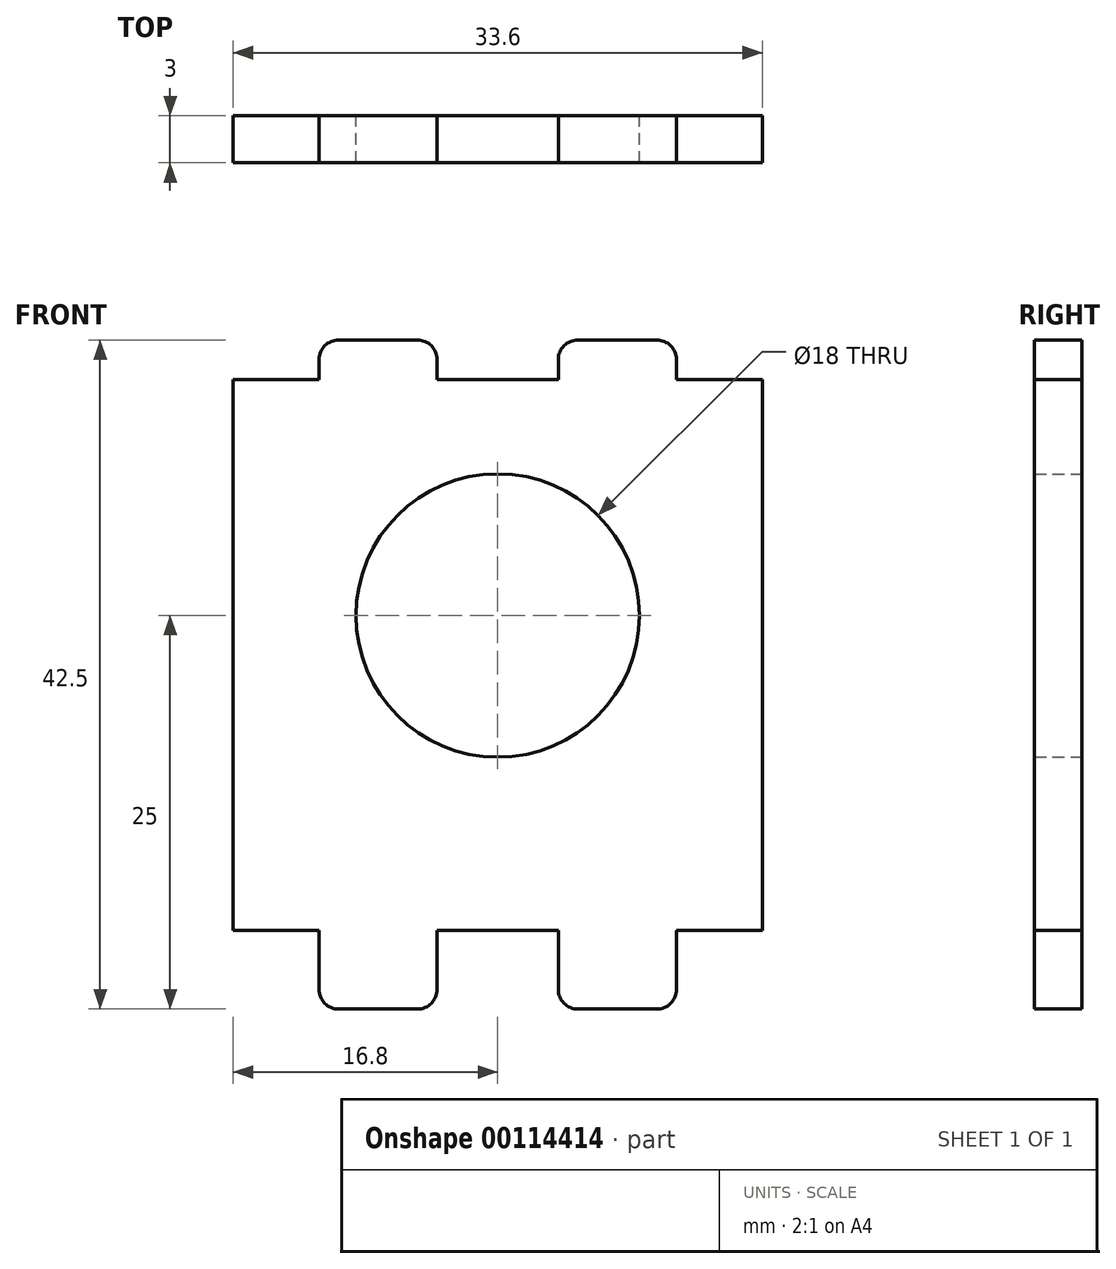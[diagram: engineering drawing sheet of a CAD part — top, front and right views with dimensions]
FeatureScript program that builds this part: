
annotation { "Feature Type Name" : "Feature", "Feature Type Description" : "" }
export const myFeature = defineFeature(function(context is Context, id is Id, definition is map)
    precondition{}
    {
        {
            var Q0;
            Q0=qCreatedBy(makeId("Front.planeOp"),FACE);
            var sketch = newSketch(context, id + "F0", { "sketchPlane" : qUnion([Q0])});
            skLineSegment(sketch, "E0.bottom", {"start": v(-16.8, 17.5) * mm, "end": v(-11.35, 17.5) * mm});
            skLineSegment(sketch, "E0.top", {"start": v(-16.8, -17.5) * mm, "end": v(-11.35, -17.5) * mm});
            skLineSegment(sketch, "E0.left", {"start": v(-16.8, 17.5) * mm, "end": v(-16.8, -17.5) * mm});
            skLineSegment(sketch, "E0.right", {"start": v(16.8, 17.5) * mm, "end": v(16.8, -17.5) * mm});
            skPoint(sketch, "E0.middle", {"position": v(0, 0) * mm});
            skLineSegment(sketch, "E1", {"start": v(-11.35, 18.75) * mm, "end": v(-11.35, 17.5) * mm});
            skLineSegment(sketch, "E2", {"start": v(11.35, 18.75) * mm, "end": v(11.35, 17.5) * mm});
            skLineSegment(sketch, "E3", {"start": v(-11.35, -17.5) * mm, "end": v(-11.35, -21.25) * mm});
            skLineSegment(sketch, "E4", {"start": v(11.35, -17.5) * mm, "end": v(11.35, -21.25) * mm});
            skLineSegment(sketch, "E5.trimOffspring", {"start": v(11.35, -17.5) * mm, "end": v(16.8, -17.5) * mm});
            skLineSegment(sketch, "E6.trimOffspring", {"start": v(11.35, 17.5) * mm, "end": v(16.8, 17.5) * mm});
            skLineSegment(sketch, "E7", {"start": v(-3.85, 17.5) * mm, "end": v(3.85, 17.5) * mm});
            skLineSegment(sketch, "E8", {"start": v(-3.85, -17.5) * mm, "end": v(3.85, -17.5) * mm});
            skLineSegment(sketch, "E9", {"start": v(-3.85, 18.75) * mm, "end": v(-3.85, 17.5) * mm});
            skLineSegment(sketch, "E10", {"start": v(3.85, 18.75) * mm, "end": v(3.85, 17.5) * mm});
            skPoint(sketch, "E10.endSnap0", {"position": v(0, 17.5) * mm});
            skLineSegment(sketch, "E11", {"start": v(-3.85, -17.5) * mm, "end": v(-3.85, -21.25) * mm});
            skLineSegment(sketch, "E12", {"start": v(3.85, -17.5) * mm, "end": v(3.85, -21.25) * mm});
            skPoint(sketch, "E13", {"position": v(-11.35, 18.75) * mm});
            skPoint(sketch, "E14", {"position": v(-3.85, 18.75) * mm});
            skPoint(sketch, "E15", {"position": v(3.85, 18.75) * mm});
            skPoint(sketch, "E16", {"position": v(11.35, 18.75) * mm});
            skPoint(sketch, "E17", {"position": v(11.35, -21.25) * mm});
            skPoint(sketch, "E18", {"position": v(3.85, -21.25) * mm});
            skPoint(sketch, "E19", {"position": v(-3.85, -21.25) * mm});
            skPoint(sketch, "E20", {"position": v(-11.35, -21.25) * mm});
            skPoint(sketch, "E21", {"position": v(-10.1, 20) * mm});
            skPoint(sketch, "E22", {"position": v(-5.1, 20) * mm});
            skPoint(sketch, "E23", {"position": v(5.1, 20) * mm});
            skPoint(sketch, "E24", {"position": v(10.1, 20) * mm});
            skPoint(sketch, "E25", {"position": v(-10.1, -22.5) * mm});
            skPoint(sketch, "E26", {"position": v(-5.1, -22.5) * mm});
            skPoint(sketch, "E27", {"position": v(5.1, -22.5) * mm});
            skPoint(sketch, "E28", {"position": v(10.1, -22.5) * mm});
            skLineSegment(sketch, "E29", {"start": v(-10.1, 20) * mm, "end": v(-5.1, 20) * mm});
            skLineSegment(sketch, "E30", {"start": v(5.1, 20) * mm, "end": v(10.1, 20) * mm});
            skLineSegment(sketch, "E31", {"start": v(-10.1, -22.5) * mm, "end": v(-5.1, -22.5) * mm});
            skLineSegment(sketch, "E32", {"start": v(5.1, -22.5) * mm, "end": v(10.1, -22.5) * mm});
            skArc(sketch, "E33", {"start": v(-10.1, 20) * mm, "mid": v(-10.98, 19.63) * mm, "end": v(-11.35, 18.75) * mm});
            skArc(sketch, "E34", {"start": v(-5.1, 20) * mm, "mid": v(-4.22, 19.63) * mm, "end": v(-3.85, 18.75) * mm});
            skArc(sketch, "E35", {"start": v(5.1, 20) * mm, "mid": v(4.22, 19.63) * mm, "end": v(3.85, 18.75) * mm});
            skArc(sketch, "E36", {"start": v(10.1, 20) * mm, "mid": v(10.98, 19.63) * mm, "end": v(11.35, 18.75) * mm});
            skArc(sketch, "E37", {"start": v(-10.1, -22.5) * mm, "mid": v(-10.98, -22.13) * mm, "end": v(-11.35, -21.25) * mm});
            skArc(sketch, "E38", {"start": v(-5.1, -22.5) * mm, "mid": v(-4.22, -22.13) * mm, "end": v(-3.85, -21.25) * mm});
            skArc(sketch, "E39", {"start": v(5.1, -22.5) * mm, "mid": v(4.22, -22.13) * mm, "end": v(3.85, -21.25) * mm});
            skArc(sketch, "E40", {"start": v(10.1, -22.5) * mm, "mid": v(10.98, -22.13) * mm, "end": v(11.35, -21.25) * mm});
            skLineSegment(sketch, "E41", {"start": v(-16.8, 2.5) * mm, "end": v(16.8, 2.5) * mm});
            skPoint(sketch, "E41.endSnap0", {"position": v(16.8, 0) * mm});
            skPoint(sketch, "E42", {"position": v(0, 2.5) * mm});
            skCircle(sketch, "E43", {"center": v(0, 2.5) * mm, "radius": 9 * mm});
            skLineSegment(sketch, "E44", {"start": v(11.35, -21.25) * mm, "end": v(3.85, -21.25) * mm});
            skLineSegment(sketch, "E45", {"start": v(-3.85, -21.25) * mm, "end": v(-11.35, -21.25) * mm});
            skSolve(sketch);
        }
        {
            var Q0;
            {var subQ1=sQuery(id+"F0.wireOp",EDGE,"E0.bottom");Q0=makeQuery(id+"F0.imprint","IMPRINT",FACE,{"disambiguationData":[TD([[makeQuery(id+"F0.imprint","IMPRINT",EDGE,{"derivedFrom":subQ1}),-1.0]])]});}
            var Q1;
            {var subQ9=sQuery(id+"F0.wireOp",EDGE,"E0.top");Q1=makeQuery(id+"F0.imprint","IMPRINT",FACE,{"disambiguationData":[TD([[makeQuery(id+"F0.imprint","IMPRINT",EDGE,{"derivedFrom":subQ9}),1.0]])]});}
            var Q2;
            Q2=makeQuery(id+"F0.imprint","IMPRINT",FACE,{"disambiguationData":[TD([[makeQuery(id+"F0.imprint","IMPRINT",EDGE,{"derivedFrom":sQuery(id+"F0.wireOp",EDGE,"E31")}),1.0]])]});
            var Q3;
            Q3=makeQuery(id+"F0.imprint","IMPRINT",FACE,{"disambiguationData":[TD([[makeQuery(id+"F0.imprint","IMPRINT",EDGE,{"derivedFrom":sQuery(id+"F0.wireOp",EDGE,"E32")}),1.0]])]});
            extrude(context, id + "F1", {"entities" : qUnion([Q0, Q1, Q2, Q3]), "depth" : 3 * mm});
        }
    });
